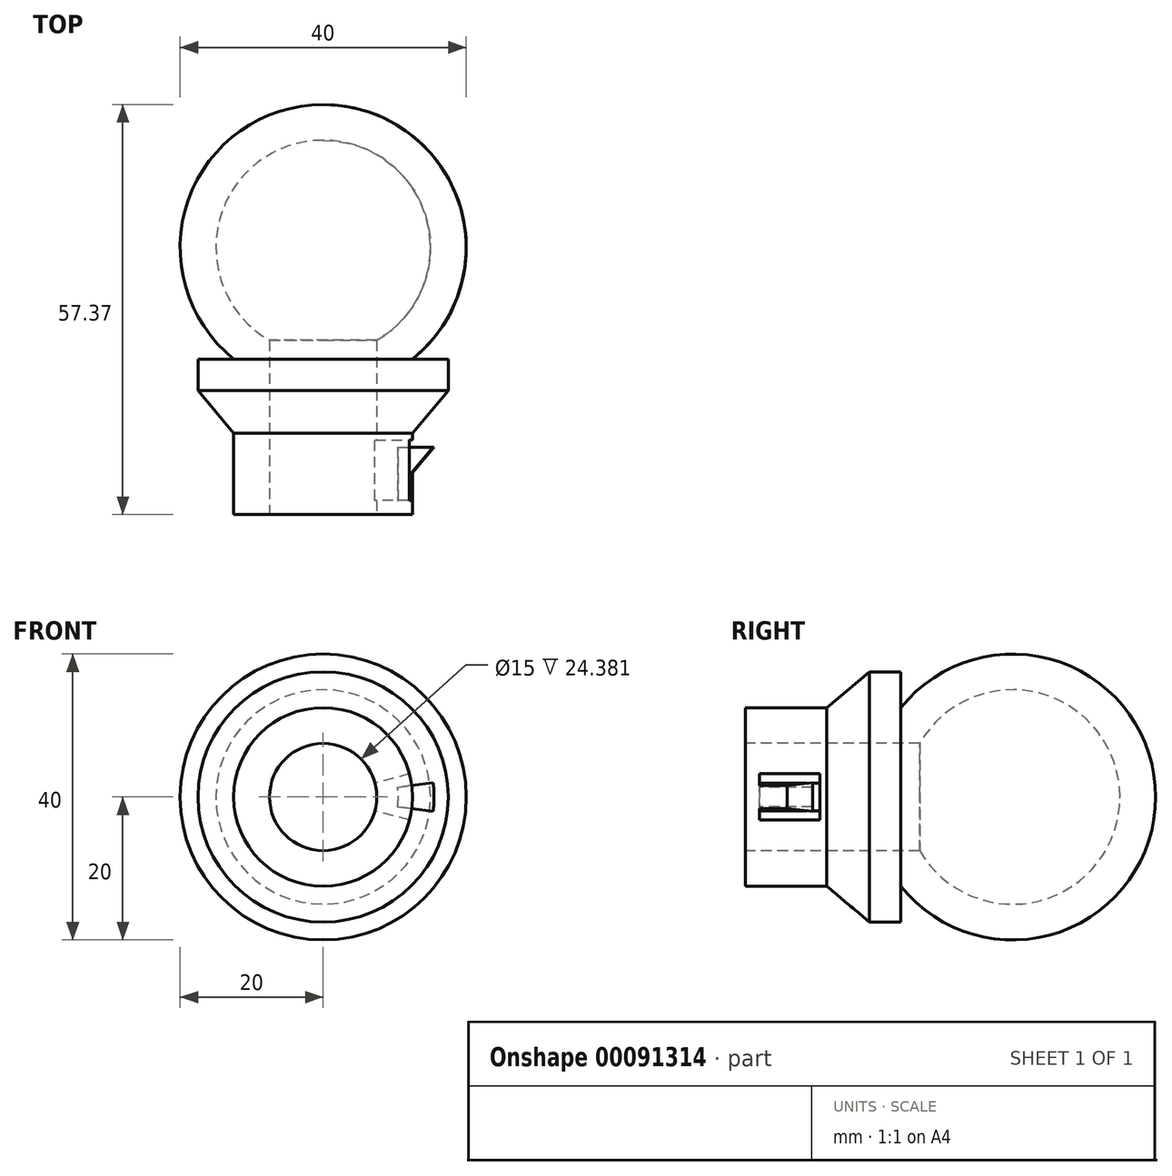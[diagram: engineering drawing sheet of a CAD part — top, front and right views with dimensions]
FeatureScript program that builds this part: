
annotation { "Feature Type Name" : "Feature", "Feature Type Description" : "" }
export const myFeature = defineFeature(function(context is Context, id is Id, definition is map)
    precondition{}
    {
        {
            var Q0;
            Q0=qCreatedBy(makeId("Top.planeOp"),FACE);
            var sketch = newSketch(context, id + "F0", { "sketchPlane" : qUnion([Q0])});
            skLineSegment(sketch, "E0", {"start": v(-12.5, 0) * mm, "end": v(-7.5, 0) * mm});
            skLineSegment(sketch, "E1", {"start": v(12.5, 0) * mm, "end": v(12.5, 21.76) * mm});
            skArc(sketch, "E2", {"start": v(7.5, 18.83) * mm, "mid": v(0, 57.37) * mm, "end": v(-7.5, 18.83) * mm});
            skLineSegment(sketch, "E3", {"start": v(0, 22.37) * mm, "end": v(0, -26.2) * mm, "construction": true});
            skLineSegment(sketch, "E4.MirrorCS", {"start": v(-12.5, 0) * mm, "end": v(-12.5, 21.76) * mm});
            skLineSegment(sketch, "E5", {"start": v(-7.5, 24.38) * mm, "end": v(-7.5, 0) * mm});
            skLineSegment(sketch, "E6.MirrorCS", {"start": v(7.5, 24.38) * mm, "end": v(7.5, 0) * mm});
            skLineSegment(sketch, "E7.trimOffspring", {"start": v(7.5, 0) * mm, "end": v(12.5, 0) * mm});
            skArc(sketch, "E8.0", {"start": v(7.5, 24.38) * mm, "mid": v(0, 52.37) * mm, "end": v(-7.5, 24.38) * mm});
            skLineSegment(sketch, "E9", {"start": v(0, 0) * mm, "end": v(0, 52.37) * mm});
            skLineSegment(sketch, "E10", {"start": v(0, 52.37) * mm, "end": v(0, 57.37) * mm});
            skLineSegment(sketch, "E11", {"start": v(12.5, 21.76) * mm, "end": v(17.5, 21.76) * mm});
            skLineSegment(sketch, "E12", {"start": v(17.5, 21.76) * mm, "end": v(17.5, 17.37) * mm});
            skLineSegment(sketch, "E13", {"start": v(17.5, 17.37) * mm, "end": v(12.5, 17.37) * mm});
            skLineSegment(sketch, "E14", {"start": v(17.5, 17.37) * mm, "end": v(12.5, 11.41) * mm});
            skSolve(sketch);
        }
        {
            var Q0;
            {var subQ6=sQuery(id+"F0.wireOp",EDGE,"E10");Q0=makeQuery(id+"F0.imprint","IMPRINT",FACE,{"disambiguationData":[TD([[makeQuery(id+"F0.imprint","IMPRINT",EDGE,{"derivedFrom":subQ6}),-1.0]])]});}
            var Q1;
            {var subQ0=sQuery(id+"F0.wireOp",EDGE,"E1");Q1=makeQuery(id+"F0.imprint","IMPRINT",FACE,{"disambiguationData":[TD([[makeQuery(id+"F0.imprint","IMPRINT",EDGE,{"derivedFrom":subQ0}),1.0]])]});}
            var Q2;
            {var subQ0=sQuery(id+"F0.wireOp",EDGE,"E11");Q2=makeQuery(id+"F0.imprint","IMPRINT",FACE,{"disambiguationData":[TD([[makeQuery(id+"F0.imprint","IMPRINT",EDGE,{"derivedFrom":subQ0}),-1.0]])]});}
            var Q3;
            {var subQ0=sQuery(id+"F0.wireOp",EDGE,"E13");Q3=makeQuery(id+"F0.imprint","IMPRINT",FACE,{"disambiguationData":[TD([[makeQuery(id+"F0.imprint","IMPRINT",EDGE,{"derivedFrom":subQ0}),1.0]])]});}
            var Q4;
            Q4=sQuery(id+"F0.wireOp",EDGE,"E9");
            revolve(context, id + "F1", {"entities" : qUnion([Q0, Q1, Q2, Q3]), "axis" : qUnion([Q4]), "revolveType" : RevolveType.FULL});
        }
        {
            var Q0;
            Q0=qCreatedBy(makeId("Top.planeOp"),FACE);
            var sketch = newSketch(context, id + "F2", { "sketchPlane" : qUnion([Q0])});
            skLineSegment(sketch, "E15", {"start": v(-12.5, 0) * mm, "end": v(-12.5, 11.41) * mm});
            skLineSegment(sketch, "E16.0", {"start": v(12.5, 0) * mm, "end": v(-12.5, 0) * mm});
            skLineSegment(sketch, "E17", {"start": v(12.5, 11.41) * mm, "end": v(12.5, 0) * mm});
            skLineSegment(sketch, "E18.0", {"start": v(7.5, 0) * mm, "end": v(-7.5, 0) * mm});
            skLineSegment(sketch, "E19", {"start": v(7.5, 0) * mm, "end": v(7.5, 10.41) * mm});
            skLineSegment(sketch, "E20", {"start": v(7.5, 10.41) * mm, "end": v(12.5, 10.41) * mm});
            skLineSegment(sketch, "E21", {"start": v(12.5, 9.41) * mm, "end": v(15.5, 9.41) * mm});
            skLineSegment(sketch, "E22", {"start": v(15.5, 9.41) * mm, "end": v(12.5, 5.84) * mm});
            skLineSegment(sketch, "E23", {"start": v(12.5, 2) * mm, "end": v(7.5, 2) * mm});
            skLineSegment(sketch, "E24", {"start": v(12.5, 9.41) * mm, "end": v(10.5, 9.41) * mm});
            skLineSegment(sketch, "E25", {"start": v(10.5, 9.41) * mm, "end": v(10.5, 2) * mm});
            skLineSegment(sketch, "E26", {"start": v(10.5, 2) * mm, "end": v(12.5, 2) * mm});
            skSolve(sketch);
        }
        {
            var Q0;
            {var subQ1=sQuery(id+"F2.wireOp",EDGE,"E20");Q0=makeQuery(id+"F2.imprint","IMPRINT",FACE,{"disambiguationData":[TD([[makeQuery(id+"F2.imprint","IMPRINT",EDGE,{"derivedFrom":subQ1}),-1.0]])]});}
            var Q1;
            {var subQ0=sQuery(id+"F2.wireOp",EDGE,"E24");Q1=makeQuery(id+"F2.imprint","IMPRINT",FACE,{"disambiguationData":[TD([[makeQuery(id+"F2.imprint","IMPRINT",EDGE,{"derivedFrom":subQ0}),1.0]])]});}
            var Q2;
            Q2=makeQuery(id+"F1.opRevolve","SWEPT_EDGE",EDGE,{"disambiguationData":[OSD([sQuery(id+"F0.wireOp",EDGE,"E1"),sQuery(id+"F0.wireOp",EDGE,"E7.trimOffspring")])]});
            revolve(context, id + "F3", {"operationType" : NewBodyOperationType.REMOVE, "entities" : qUnion([Q0, Q1]), "axis" : qUnion([Q2]), "revolveType" : RevolveType.SYMMETRIC, "oppositeDirection" : true, "angle" : 30 * degree});
        }
        {
            var Q0;
            {var subQ0=sQuery(id+"F2.wireOp",EDGE,"E21");Q0=makeQuery(id+"F2.imprint","IMPRINT",FACE,{"disambiguationData":[TD([[makeQuery(id+"F2.imprint","IMPRINT",EDGE,{"derivedFrom":subQ0}),-1.0]])]});}
            var Q1;
            {var subQ0=sQuery(id+"F2.wireOp",EDGE,"E24");Q1=makeQuery(id+"F2.imprint","IMPRINT",FACE,{"disambiguationData":[TD([[makeQuery(id+"F2.imprint","IMPRINT",EDGE,{"derivedFrom":subQ0}),1.0]])]});}
            var Q2;
            Q2=makeQuery(id+"F1.opRevolve","SWEPT_EDGE",EDGE,{"disambiguationData":[OSD([sQuery(id+"F0.wireOp",EDGE,"E1"),sQuery(id+"F0.wireOp",EDGE,"E7.trimOffspring")])]});
            revolve(context, id + "F4", {"operationType" : NewBodyOperationType.ADD, "entities" : qUnion([Q0, Q1]), "axis" : qUnion([Q2]), "revolveType" : RevolveType.SYMMETRIC, "angle" : 15 * degree});
        }
    });
